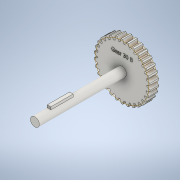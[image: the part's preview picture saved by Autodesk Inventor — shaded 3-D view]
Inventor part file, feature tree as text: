
AUTODESK INVENTOR PART (.ipt)
format: ipt  version: 2021 (Build 250183000, 183)  size: 622,080 bytes
history: native  units: mm (DEFAULTED — no unit token found)
features: sketch x8, extrude x5, plane x3, other x3, emboss x1
ambient origin geometry x8: Origin, YZ Plane, XZ Plane, XY Plane, X Axis, Y Axis, Z Axis, Center Point
bodies: Solid1 (feature_tree)
feature tree (20):
  extrude  "Extrusion1"  Depth=5.0mm TaperAngle=0.0deg
  plane  "Work Plane2"
  plane  "Work Plane8"
  plane  "Work Plane9"
  other  "Spur Gear"
  extrude  "Extrusion3"  Depth=10.0mm TaperAngle=0.0deg
  sketch  "Sketch6"  dims[d39=0.0mm d41=0.0mm]
  extrude  "Extrusion4"  Depth=1.047198mm TaperAngle=0.0deg
  extrude  "Extrusion5"  TaperAngle=0.0deg  [1 undecoded]
  extrude  "Extrusion6"  Depth=22.5mm
  emboss  "Emboss1"
  sketch  "Sketch1"  dims[d0=31.6mm d1=5.0mm d2=0.0mm]
  sketch  "Sketch2"  dims[d3=30.0mm d4=10.0mm d5=0.0mm]
  other  "Srf1"
  sketch  "Sketch5"  dims[d16=22.5mm d17=0.0mm d34=1.047198mm]
  sketch  "Sketch7"  dims[d43=22.5mm d46=22.5mm]
  sketch  "Sketch8"  dims[d47=0.0mm d48=0.0mm]
  sketch  "Sketch9"  dims[d63=5.0mm]
  sketch  "Sketch10"  dims[d68=41.0mm d69=0.0mm d70=2.0mm d71=1.5mm d72=12.5mm d73=0.0mm d74=5.0mm d75=8.0mm d76=0.0mm d77=8.0mm d78=0.0mm d79=1.0mm d80=0.0mm d59=0.5mm d60=0.872665mm d61=0.5mm d62=0.872665mm]
  other  "Pitch Diameter"
note: 1 required parameter value undecoded (feature->parameter linkage not recoverable at this tier; creation-order binding heuristic only, values carry confidence <= 0.55)
